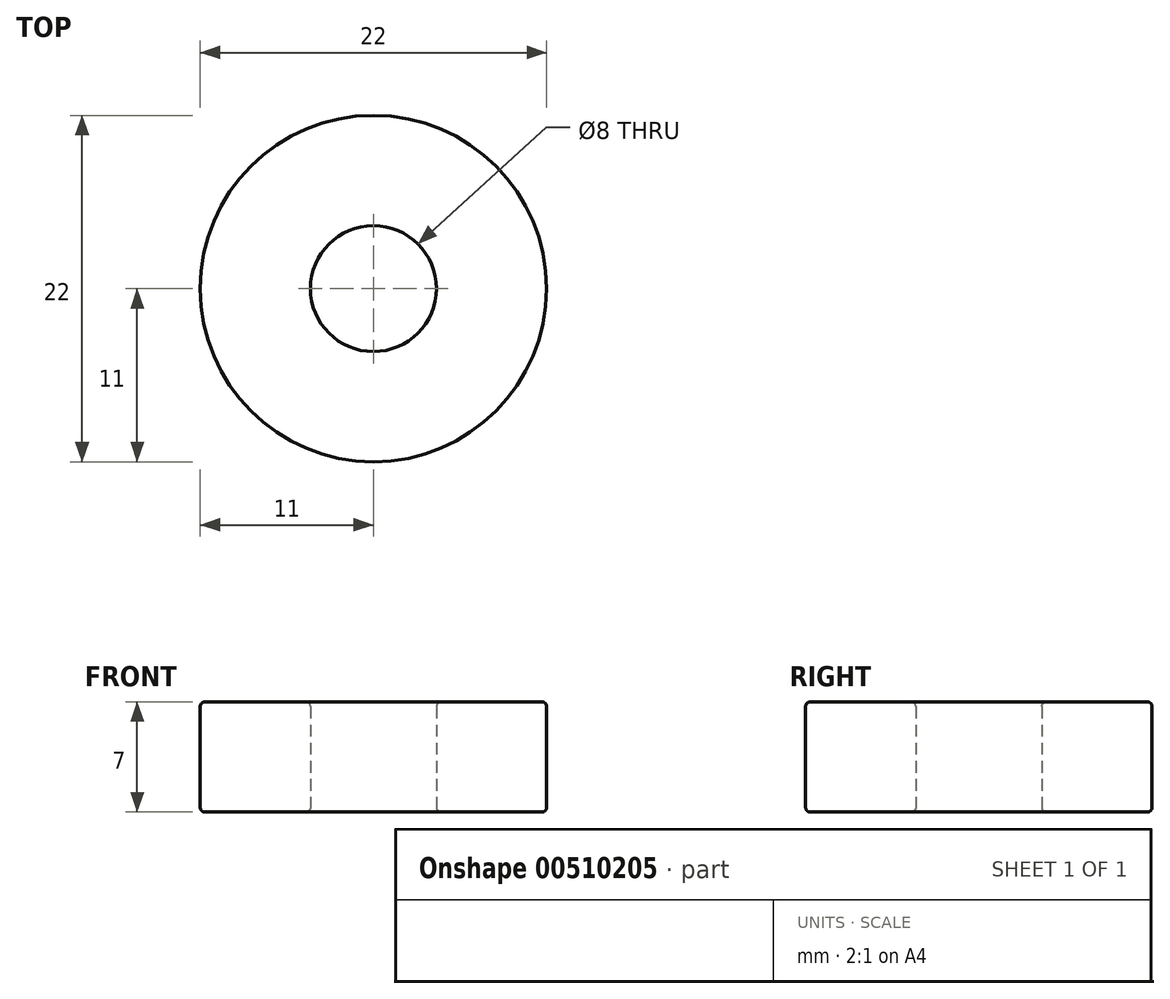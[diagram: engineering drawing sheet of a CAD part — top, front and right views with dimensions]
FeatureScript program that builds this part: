
annotation { "Feature Type Name" : "Feature", "Feature Type Description" : "" }
export const myFeature = defineFeature(function(context is Context, id is Id, definition is map)
    precondition{}
    {
        {
            var Q0;
            Q0=qCreatedBy(makeId("Top.planeOp"),FACE);
            var sketch = newSketch(context, id + "F0", { "sketchPlane" : qUnion([Q0])});
            skCircle(sketch, "E0", {"center": v(0, 0) * mm, "radius": 4 * mm});
            skCircle(sketch, "E1", {"center": v(0, 0) * mm, "radius": 11 * mm});
            skSolve(sketch);
        }
        {
            var Q0;
            Q0=makeQuery(id+"F0.imprint","IMPRINT",FACE,{"disambiguationData":[TD([[makeQuery(id+"F0.imprint","IMPRINT",EDGE,{"derivedFrom":sQuery(id+"F0.wireOp",EDGE,"E0")}),-1.0]])]});
            extrude(context, id + "F1", {"entities" : qUnion([Q0]), "depth" : 7 * mm, "offsetDistance" : 25 * mm});
        }
        {
            var Q0;
            Q0=makeQuery(id+"F1.opExtrude","CAP_EDGE",EDGE,{"disambiguationData":[OSD([sQuery(id+"F0.wireOp",EDGE,"E1")])],"isStart":false});
            var Q1;
            Q1=makeQuery(id+"F1.opExtrude","CAP_EDGE",EDGE,{"disambiguationData":[OSD([sQuery(id+"F0.wireOp",EDGE,"E0")])],"isStart":false});
            var Q2;
            Q2=makeQuery(id+"F1.opExtrude","CAP_EDGE",EDGE,{"disambiguationData":[OSD([sQuery(id+"F0.wireOp",EDGE,"E1")])],"isStart":true});
            var Q3;
            Q3=makeQuery(id+"F1.opExtrude","CAP_EDGE",EDGE,{"disambiguationData":[OSD([sQuery(id+"F0.wireOp",EDGE,"E0")])],"isStart":true});
            fillet(context, id + "F2", {"entities" : qUnion([Q0, Q1, Q2, Q3]), "radius" : .3 * mm, "tangentPropagation" : true, "allowEdgeOverflow" : false});
        }
    });
